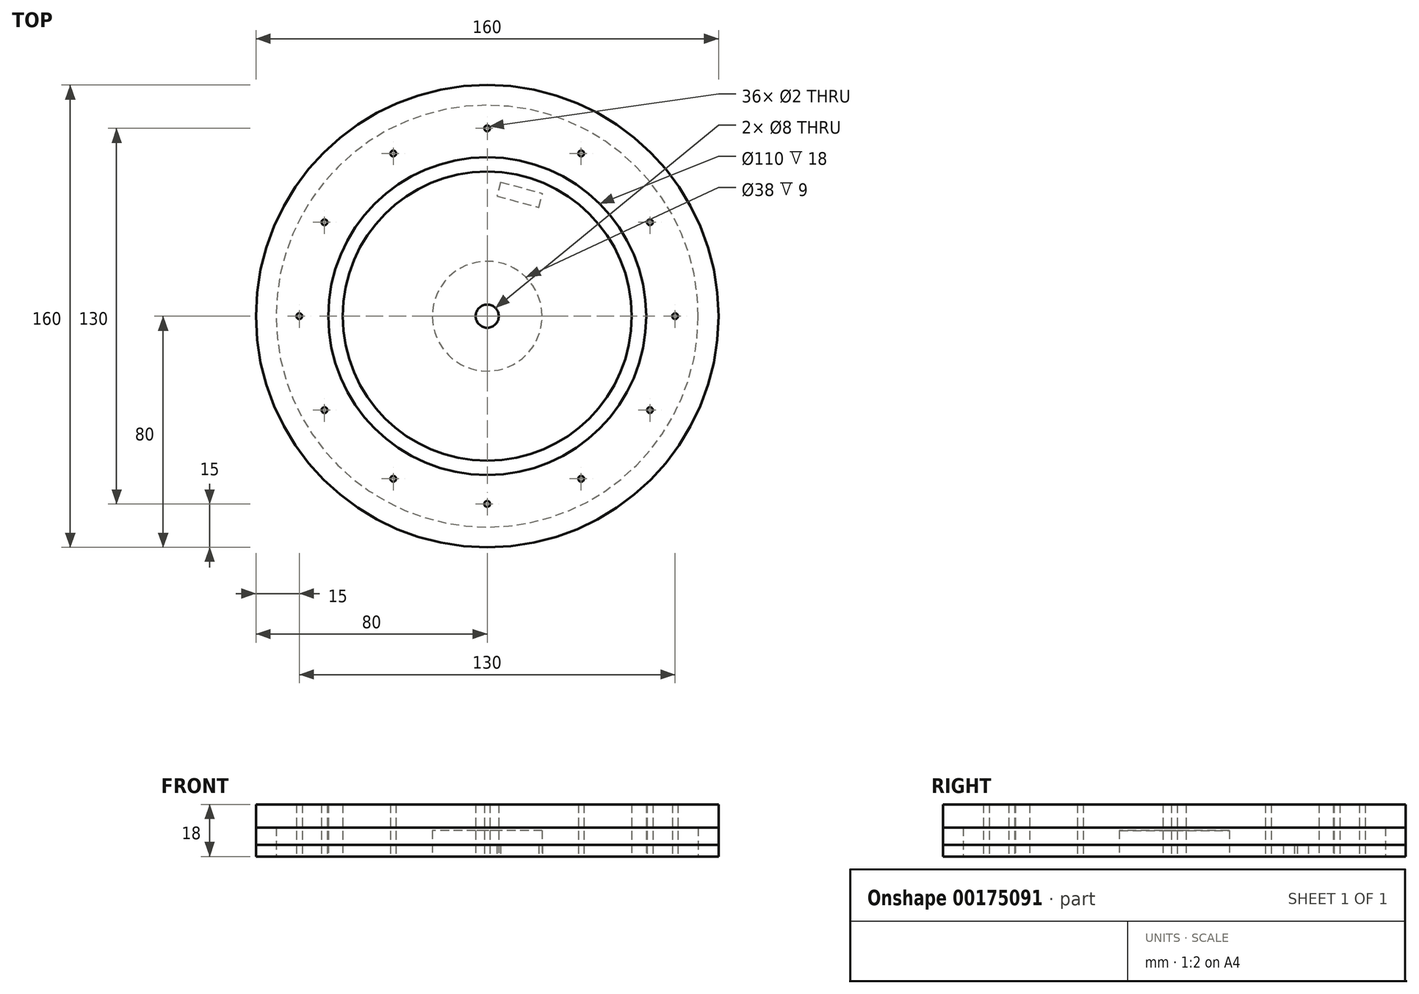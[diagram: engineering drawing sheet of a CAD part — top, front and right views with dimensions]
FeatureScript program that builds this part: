
annotation { "Feature Type Name" : "Feature", "Feature Type Description" : "" }
export const myFeature = defineFeature(function(context is Context, id is Id, definition is map)
    precondition{}
    {
        {
            var Q0;
            Q0=qCreatedBy(makeId("Top.planeOp"),FACE);
            var sketch = newSketch(context, id + "F0", { "sketchPlane" : qUnion([Q0])});
            skCircle(sketch, "E0", {"center": v(0, 0) * mm, "radius": 50 * mm});
            skCircle(sketch, "E1", {"center": v(0, 0) * mm, "radius": 19 * mm});
            skCircle(sketch, "E2", {"center": v(0, 0) * mm, "radius": 4 * mm});
            skCircle(sketch, "E3", {"center": v(0, 0) * mm, "radius": 55 * mm});
            skCircle(sketch, "E4", {"center": v(0, 0) * mm, "radius": 73 * mm});
            skCircle(sketch, "E5", {"center": v(0, 0) * mm, "radius": 80 * mm});
            skCircle(sketch, "E6", {"center": v(0, 0) * mm, "radius": 65 * mm, "construction": true});
            skLineSegment(sketch, "E7", {"start": v(0, 0) * mm, "end": v(0, 65) * mm, "construction": true});
            skCircle(sketch, "E8", {"center": v(0, 65) * mm, "radius": 1 * mm});
            skCircle(sketch, "E9.1.0", {"center": v(-32.5, 56.3) * mm, "radius": 1 * mm});
            skCircle(sketch, "E9.2.0", {"center": v(-56.3, 32.5) * mm, "radius": 1 * mm});
            skCircle(sketch, "E9.3.0", {"center": v(-65, 0) * mm, "radius": 1 * mm});
            skCircle(sketch, "E9.4.0", {"center": v(-56.3, -32.5) * mm, "radius": 1 * mm});
            skCircle(sketch, "E9.5.0", {"center": v(-32.5, -56.3) * mm, "radius": 1 * mm});
            skCircle(sketch, "E10.1.6.0", {"center": v(0, -65) * mm, "radius": 1 * mm});
            skCircle(sketch, "E10.1.7.0", {"center": v(32.5, -56.3) * mm, "radius": 1 * mm});
            skCircle(sketch, "E10.1.8.0", {"center": v(56.3, -32.5) * mm, "radius": 1 * mm});
            skCircle(sketch, "E10.1.9.0", {"center": v(65, 0) * mm, "radius": 1 * mm});
            skCircle(sketch, "E10.1.10.0", {"center": v(56.3, 32.5) * mm, "radius": 1 * mm});
            skCircle(sketch, "E10.1.11.0", {"center": v(32.5, 56.3) * mm, "radius": 1 * mm});
            skLineSegment(sketch, "E11", {"start": v(0, 0) * mm, "end": v(20.7, 77.27) * mm, "construction": true});
            skLineSegment(sketch, "E12", {"start": v(4.66, 46.37) * mm, "end": v(3.37, 41.54) * mm});
            skLineSegment(sketch, "E13", {"start": v(3.37, 41.54) * mm, "end": v(17.86, 37.66) * mm});
            skLineSegment(sketch, "E14", {"start": v(17.86, 37.66) * mm, "end": v(19.15, 42.5) * mm});
            skLineSegment(sketch, "E15", {"start": v(4.66, 46.37) * mm, "end": v(19.15, 42.5) * mm});
            skLineSegment(sketch, "E16", {"start": v(4.66, 46.37) * mm, "end": v(11.26, 42.02) * mm, "construction": true});
            skLineSegment(sketch, "E17", {"start": v(11.26, 42.02) * mm, "end": v(17.86, 37.66) * mm, "construction": true});
            skSolve(sketch);
        }
        {
            var Q0;
            Q0=makeQuery(id+"F0.imprint","IMPRINT",FACE,{"disambiguationData":[TD([[makeQuery(id+"F0.imprint","IMPRINT",EDGE,{"derivedFrom":sQuery(id+"F0.wireOp",EDGE,"E0")}),1.0]])]});
            var Q1;
            Q1=makeQuery(id+"F0.imprint","IMPRINT",FACE,{"disambiguationData":[TD([[makeQuery(id+"F0.imprint","IMPRINT",EDGE,{"derivedFrom":sQuery(id+"F0.wireOp",EDGE,"E1")}),1.0]])]});
            var Q2;
            Q2=makeQuery(id+"F0.imprint","IMPRINT",FACE,{"disambiguationData":[TD([[makeQuery(id+"F0.imprint","IMPRINT",EDGE,{"derivedFrom":sQuery(id+"F0.wireOp",EDGE,"E12")}),1.0]])]});
            extrude(context, id + "F1", {"entities" : qUnion([Q0, Q1, Q2]), "depth" : 18 * mm});
        }
        {
            var Q0;
            Q0=makeQuery(id+"F0.imprint","IMPRINT",FACE,{"disambiguationData":[TD([[makeQuery(id+"F0.imprint","IMPRINT",EDGE,{"derivedFrom":sQuery(id+"F0.wireOp",EDGE,"E1")}),1.0]])]});
            extrude(context, id + "F2", {"entities" : qUnion([Q0]), "operationType" : NewBodyOperationType.REMOVE, "depth" : 9 * mm});
        }
        {
            var Q0;
            Q0=makeQuery(id+"F0.imprint","IMPRINT",FACE,{"disambiguationData":[TD([[makeQuery(id+"F0.imprint","IMPRINT",EDGE,{"derivedFrom":sQuery(id+"F0.wireOp",EDGE,"E4")}),-1.0]])]});
            var Q1;
            Q1=makeQuery(id+"F0.imprint","IMPRINT",FACE,{"disambiguationData":[TD([[makeQuery(id+"F0.imprint","IMPRINT",EDGE,{"derivedFrom":sQuery(id+"F0.wireOp",EDGE,"E3")}),-1.0]])]});
            var Q2;
            Q2=makeQuery(id+"F0.imprint","IMPRINT",FACE,{"disambiguationData":[TD([[makeQuery(id+"F0.imprint","IMPRINT",EDGE,{"derivedFrom":sQuery(id+"F0.wireOp",EDGE,"E0")}),-1.0]])]});
            var Q3;
            Q3=makeQuery(id+"F0.imprint","IMPRINT",FACE,{"disambiguationData":[TD([[makeQuery(id+"F0.imprint","IMPRINT",EDGE,{"derivedFrom":sQuery(id+"F0.wireOp",EDGE,"E0")}),1.0]])]});
            var Q4;
            Q4=makeQuery(id+"F0.imprint","IMPRINT",FACE,{"disambiguationData":[TD([[makeQuery(id+"F0.imprint","IMPRINT",EDGE,{"derivedFrom":sQuery(id+"F0.wireOp",EDGE,"E1")}),1.0]])]});
            var Q5;
            Q5=makeQuery(id+"F0.imprint","IMPRINT",FACE,{"disambiguationData":[TD([[makeQuery(id+"F0.imprint","IMPRINT",EDGE,{"derivedFrom":sQuery(id+"F0.wireOp",EDGE,"E12")}),1.0]])]});
            extrude(context, id + "F3", {"entities" : qUnion([Q0, Q1, Q2, Q3, Q4, Q5]), "depth" : 18 * mm});
        }
        {
            var Q0;
            Q0=makeQuery(id+"F0.imprint","IMPRINT",FACE,{"disambiguationData":[TD([[makeQuery(id+"F0.imprint","IMPRINT",EDGE,{"derivedFrom":sQuery(id+"F0.wireOp",EDGE,"E4")}),-1.0]])]});
            extrude(context, id + "F4", {"entities" : qUnion([Q0]), "operationType" : NewBodyOperationType.REMOVE, "depth" : 10 * mm});
        }
        {
            var Q0;
            Q0=makeQuery(id+"F0.imprint","IMPRINT",FACE,{"disambiguationData":[TD([[makeQuery(id+"F0.imprint","IMPRINT",EDGE,{"derivedFrom":sQuery(id+"F0.wireOp",EDGE,"E4")}),-1.0]])]});
            var Q1;
            Q1=makeQuery(id+"F0.imprint","IMPRINT",FACE,{"disambiguationData":[TD([[makeQuery(id+"F0.imprint","IMPRINT",EDGE,{"derivedFrom":sQuery(id+"F0.wireOp",EDGE,"E3")}),-1.0]])]});
            extrude(context, id + "F5", {"entities" : qUnion([Q0, Q1]), "depth" : 18 * mm});
        }
        {
            var Q0;
            Q0=makeQuery(id+"F0.imprint","IMPRINT",FACE,{"disambiguationData":[TD([[makeQuery(id+"F0.imprint","IMPRINT",EDGE,{"derivedFrom":sQuery(id+"F0.wireOp",EDGE,"E4")}),-1.0]])]});
            var Q1;
            Q1=makeQuery(id+"F0.imprint","IMPRINT",FACE,{"disambiguationData":[TD([[makeQuery(id+"F0.imprint","IMPRINT",EDGE,{"derivedFrom":sQuery(id+"F0.wireOp",EDGE,"E3")}),-1.0]])]});
            var Q2;
            Q2=makeQuery(id+"F0.imprint","IMPRINT",FACE,{"disambiguationData":[TD([[makeQuery(id+"F0.imprint","IMPRINT",EDGE,{"derivedFrom":sQuery(id+"F0.wireOp",EDGE,"E0")}),-1.0]])]});
            var Q3;
            Q3=makeQuery(id+"F0.imprint","IMPRINT",FACE,{"disambiguationData":[TD([[makeQuery(id+"F0.imprint","IMPRINT",EDGE,{"derivedFrom":sQuery(id+"F0.wireOp",EDGE,"E0")}),1.0]])]});
            var Q4;
            Q4=makeQuery(id+"F0.imprint","IMPRINT",FACE,{"disambiguationData":[TD([[makeQuery(id+"F0.imprint","IMPRINT",EDGE,{"derivedFrom":sQuery(id+"F0.wireOp",EDGE,"E1")}),1.0]])]});
            var Q5;
            Q5=makeQuery(id+"F0.imprint","IMPRINT",FACE,{"disambiguationData":[TD([[makeQuery(id+"F0.imprint","IMPRINT",EDGE,{"derivedFrom":sQuery(id+"F0.wireOp",EDGE,"E2")}),1.0]])]});
            extrude(context, id + "F6", {"entities" : qUnion([Q0, Q1, Q2, Q3, Q4, Q5]), "depth" : 4 * mm});
        }
    });
